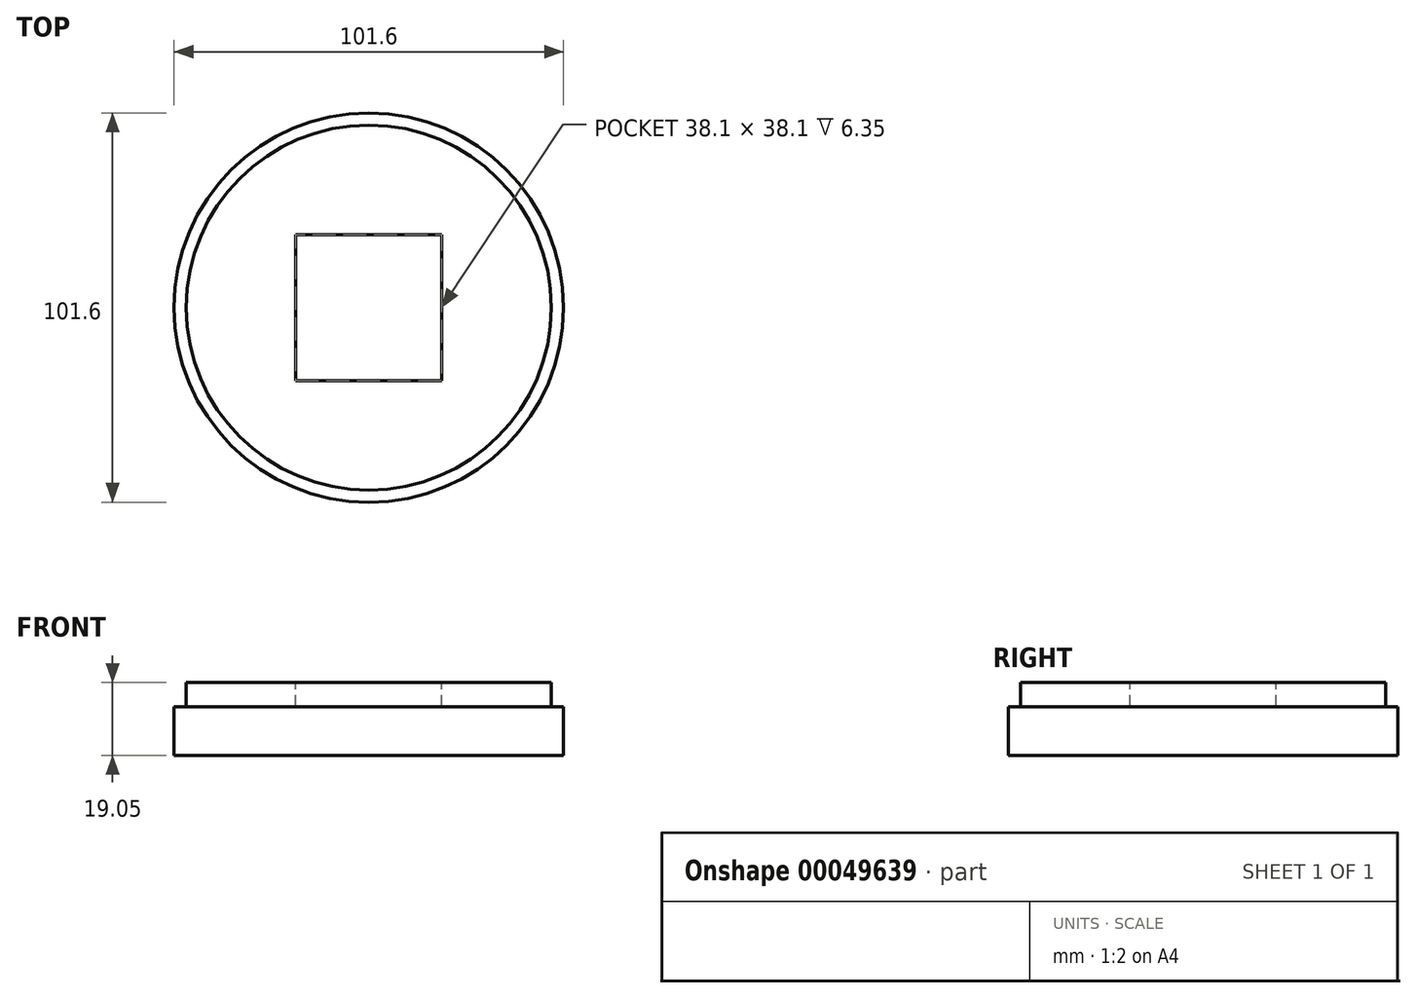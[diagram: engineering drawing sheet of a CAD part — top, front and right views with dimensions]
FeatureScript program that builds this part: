
annotation { "Feature Type Name" : "Feature", "Feature Type Description" : "" }
export const myFeature = defineFeature(function(context is Context, id is Id, definition is map)
    precondition{}
    {
        {
            var Q0;
            Q0=qCreatedBy(makeId("Top.planeOp"),FACE);
            var sketch = newSketch(context, id + "F0", { "sketchPlane" : qUnion([Q0])});
            skCircle(sketch, "E0", {"center": v(0, 0) * mm, "radius": 50.8 * mm});
            skSolve(sketch);
        }
        {
            var Q0;
            Q0=makeQuery(id+"F0.imprint","IMPRINT",FACE,{"disambiguationData":[TD([[makeQuery(id+"F0.imprint","IMPRINT",EDGE,{"derivedFrom":sQuery(id+"F0.wireOp",EDGE,"E0")}),1.0]])]});
            extrude(context, id + "F1", {"entities" : qUnion([Q0]), "depth" : 12.7 * mm});
        }
        {
            var Q0;
            Q0=makeQuery(id+"F1.opExtrude","CAP_FACE",FACE,{"disambiguationData":[OSD([sQuery(id+"F0.wireOp",EDGE,"E0")])],"isStart":false});
            var sketch = newSketch(context, id + "F2", { "sketchPlane" : qUnion([Q0])});
            skCircle(sketch, "E1", {"center": v(0, 0) * mm, "radius": 47.63 * mm});
            skSolve(sketch);
        }
        {
            var Q0;
            Q0=makeQuery(id+"F2.imprint","IMPRINT",FACE,{"disambiguationData":[TD([[makeQuery(id+"F2.imprint","IMPRINT",EDGE,{"derivedFrom":sQuery(id+"F2.wireOp",EDGE,"E1")}),1.0]])]});
            extrude(context, id + "F3", {"entities" : qUnion([Q0]), "operationType" : NewBodyOperationType.ADD, "depth" : 6.35 * mm});
        }
        {
            var Q0;
            Q0=makeQuery(id+"F3.opExtrude","CAP_FACE",FACE,{"disambiguationData":[OSD([sQuery(id+"F2.wireOp",EDGE,"E1")])],"isStart":false});
            var sketch = newSketch(context, id + "F4", { "sketchPlane" : qUnion([Q0])});
            skLineSegment(sketch, "E2.rect.bottom", {"start": v(19.05, -19.05) * mm, "end": v(-19.05, -19.05) * mm});
            skLineSegment(sketch, "E2.rect.top", {"start": v(19.05, 19.05) * mm, "end": v(-19.05, 19.05) * mm});
            skLineSegment(sketch, "E2.rect.left", {"start": v(19.05, -19.05) * mm, "end": v(19.05, 19.05) * mm});
            skLineSegment(sketch, "E2.rect.right", {"start": v(-19.05, -19.05) * mm, "end": v(-19.05, 19.05) * mm});
            skPoint(sketch, "E2.rect.middle", {"position": v(0, 0) * mm});
            skSolve(sketch);
        }
        {
            var Q0;
            Q0=makeQuery(id+"F4.imprint","IMPRINT",FACE,{"disambiguationData":[TD([[makeQuery(id+"F4.imprint","IMPRINT",EDGE,{"derivedFrom":sQuery(id+"F4.wireOp",EDGE,"E2.rect.bottom")}),-1.0]])]});
            extrude(context, id + "F5", {"entities" : qUnion([Q0]), "operationType" : NewBodyOperationType.REMOVE, "oppositeDirection" : true, "depth" : 6.35 * mm});
        }
    });
